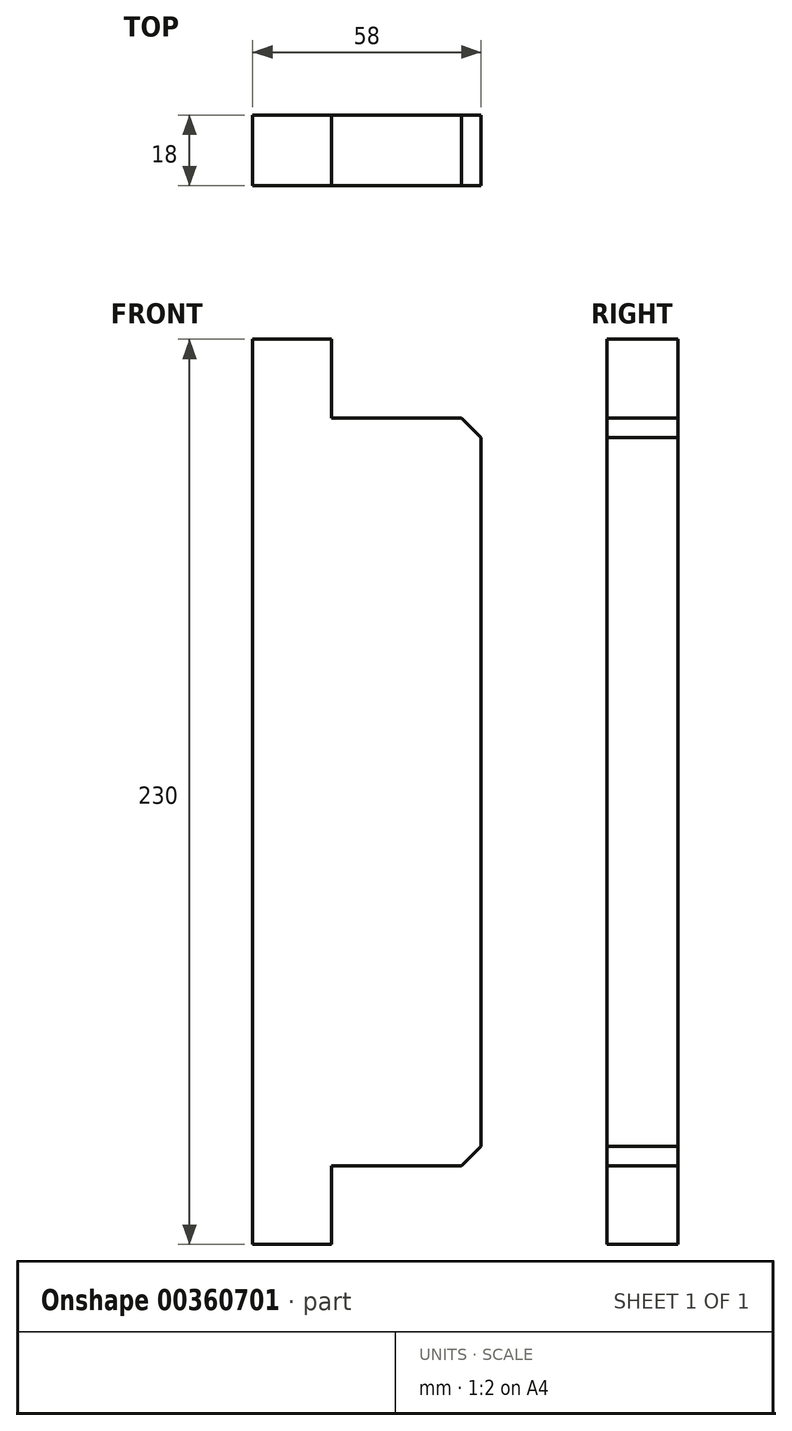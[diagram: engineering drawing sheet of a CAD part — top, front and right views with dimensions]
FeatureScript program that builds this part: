
annotation { "Feature Type Name" : "Feature", "Feature Type Description" : "" }
export const myFeature = defineFeature(function(context is Context, id is Id, definition is map)
    precondition{}
    {
        {
            var Q0;
            Q0=qCreatedBy(makeId("Front.planeOp"),FACE);
            var sketch = newSketch(context, id + "F0", { "sketchPlane" : qUnion([Q0])});
            skLineSegment(sketch, "E0.bottom", {"start": v(0, 0) * mm, "end": v(20, 0) * mm});
            skLineSegment(sketch, "E0.top", {"start": v(0, 230) * mm, "end": v(20, 230) * mm});
            skLineSegment(sketch, "E0.left", {"start": v(0, 0) * mm, "end": v(0, 230) * mm});
            skLineSegment(sketch, "E0.right", {"start": v(20, 0) * mm, "end": v(20, 20) * mm});
            skLineSegment(sketch, "E1.bottom", {"start": v(20, 210) * mm, "end": v(58, 210) * mm});
            skLineSegment(sketch, "E1.top", {"start": v(20, 20) * mm, "end": v(58, 20) * mm});
            skLineSegment(sketch, "E1.right", {"start": v(58, 210) * mm, "end": v(58, 20) * mm});
            skLineSegment(sketch, "E2.trimOffspring", {"start": v(20, 210) * mm, "end": v(20, 230) * mm});
            skSolve(sketch);
        }
        {
            var Q0;
            Q0=makeQuery(id+"F0.imprint","IMPRINT",FACE,{"disambiguationData":[TD([[makeQuery(id+"F0.imprint","IMPRINT",EDGE,{"derivedFrom":sQuery(id+"F0.wireOp",EDGE,"E0.bottom")}),1.0]])]});
            extrude(context, id + "F1", {"entities" : qUnion([Q0]), "depth" : 18 * mm});
        }
        {
            var Q0;
            Q0=makeQuery(id+"F1.opExtrude","SWEPT_EDGE",EDGE,{"disambiguationData":[OSD([sQuery(id+"F0.wireOp",EDGE,"E1.bottom"),sQuery(id+"F0.wireOp",EDGE,"E1.right")])]});
            var Q1;
            Q1=makeQuery(id+"F1.opExtrude","SWEPT_EDGE",EDGE,{"disambiguationData":[OSD([sQuery(id+"F0.wireOp",EDGE,"E1.top"),sQuery(id+"F0.wireOp",EDGE,"E1.right")])]});
            chamfer(context, id + "F2", {"entities" : qUnion([Q0, Q1]), "width" : 5 * mm, "tangentPropagation" : true});
        }
    });
